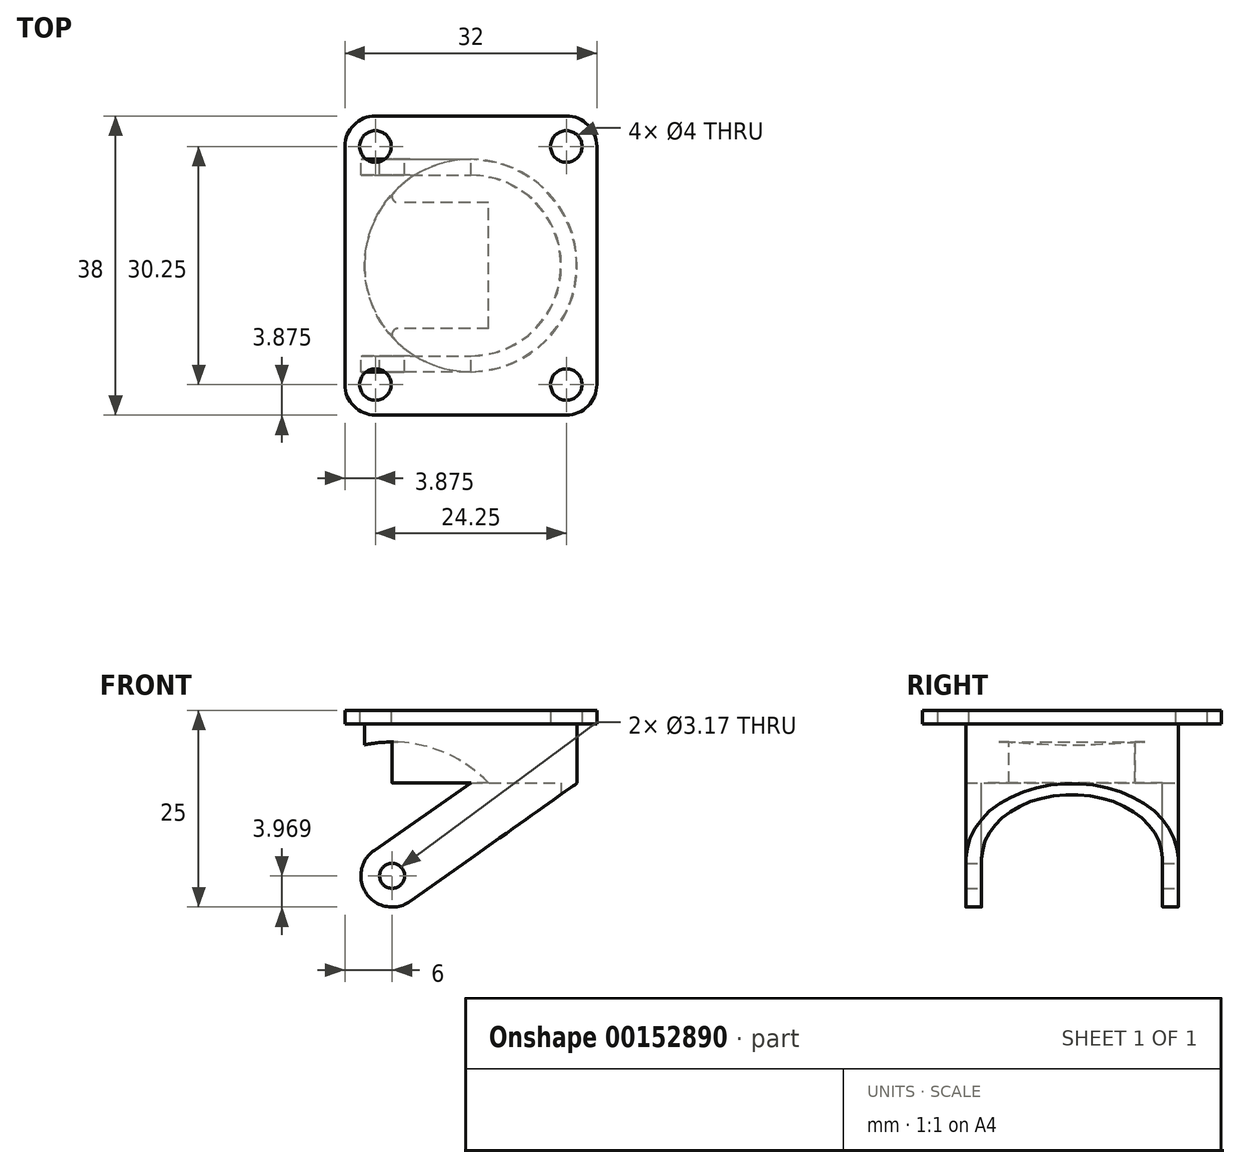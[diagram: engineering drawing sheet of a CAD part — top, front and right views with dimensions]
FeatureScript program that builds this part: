
annotation { "Feature Type Name" : "Feature", "Feature Type Description" : "" }
export const myFeature = defineFeature(function(context is Context, id is Id, definition is map)
    precondition{}
    {
        {
            var Q0;
            Q0=qCreatedBy(makeId("Top.planeOp"),FACE);
            var sketch = newSketch(context, id + "F0", { "sketchPlane" : qUnion([Q0])});
            skLineSegment(sketch, "E0.bottom", {"start": v(16, 19) * mm, "end": v(-16, 19) * mm});
            skLineSegment(sketch, "E0.top", {"start": v(16, -19) * mm, "end": v(-16, -19) * mm});
            skLineSegment(sketch, "E0.left", {"start": v(16, 19) * mm, "end": v(16, -19) * mm});
            skLineSegment(sketch, "E0.right", {"start": v(-16, 19) * mm, "end": v(-16, -19) * mm});
            skPoint(sketch, "E0.middle", {"position": v(0, 0) * mm});
            skLineSegment(sketch, "E1.bottom", {"start": v(12.12, 15.12) * mm, "end": v(-12.12, 15.12) * mm, "construction": true});
            skLineSegment(sketch, "E1.top", {"start": v(12.12, -15.12) * mm, "end": v(-12.12, -15.13) * mm, "construction": true});
            skLineSegment(sketch, "E1.left", {"start": v(12.12, 15.12) * mm, "end": v(12.13, -15.12) * mm, "construction": true});
            skLineSegment(sketch, "E1.right", {"start": v(-12.12, 15.12) * mm, "end": v(-12.12, -15.12) * mm, "construction": true});
            skLineSegment(sketch, "E2", {"start": v(12.12, 15.12) * mm, "end": v(12.12, 19) * mm, "construction": true});
            skLineSegment(sketch, "E3", {"start": v(12.12, 15.12) * mm, "end": v(16, 15.12) * mm, "construction": true});
            skCircle(sketch, "E4", {"center": v(12.12, 15.12) * mm, "radius": 2 * mm});
            skCircle(sketch, "E5", {"center": v(-12.12, 15.12) * mm, "radius": 2 * mm});
            skCircle(sketch, "E6", {"center": v(-12.12, -15.13) * mm, "radius": 2 * mm});
            skCircle(sketch, "E7", {"center": v(12.12, -15.12) * mm, "radius": 2 * mm});
            skSolve(sketch);
        }
        {
            var Q0;
            Q0 = qSketchRegion(id + "F0", true);
            extrude(context, id + "F1", {"entities" : qUnion([Q0]), "depth" : 1.75 * mm});
        }
        {
            var Q0;
            Q0=makeQuery(id+"F1.opExtrude","SWEPT_EDGE",EDGE,{"disambiguationData":[OSD([sQuery(id+"F0.wireOp",EDGE,"E0.bottom"),sQuery(id+"F0.wireOp",EDGE,"E0.left")])]});
            var Q1;
            Q1=makeQuery(id+"F1.opExtrude","SWEPT_EDGE",EDGE,{"disambiguationData":[OSD([sQuery(id+"F0.wireOp",EDGE,"E0.top"),sQuery(id+"F0.wireOp",EDGE,"E0.left")])]});
            var Q2;
            Q2=makeQuery(id+"F1.opExtrude","SWEPT_EDGE",EDGE,{"disambiguationData":[OSD([sQuery(id+"F0.wireOp",EDGE,"E0.top"),sQuery(id+"F0.wireOp",EDGE,"E0.right")])]});
            var Q3;
            Q3=makeQuery(id+"F1.opExtrude","SWEPT_EDGE",EDGE,{"disambiguationData":[OSD([sQuery(id+"F0.wireOp",EDGE,"E0.bottom"),sQuery(id+"F0.wireOp",EDGE,"E0.right")])]});
            fillet(context, id + "F2", {"entities" : qUnion([Q0, Q1, Q2, Q3]), "radius" : 3.87 * mm, "tangentPropagation" : true, "allowEdgeOverflow" : false});
        }
        {
            var Q0;
            Q0=makeQuery(id+"F1.opExtrude","CAP_FACE",FACE,{"disambiguationData":[OSD([sQuery(id+"F0.wireOp",EDGE,"E0.bottom"),sQuery(id+"F0.wireOp",EDGE,"E0.top"),sQuery(id+"F0.wireOp",EDGE,"E0.left"),sQuery(id+"F0.wireOp",EDGE,"E0.right"),sQuery(id+"F0.wireOp",EDGE,"E4"),sQuery(id+"F0.wireOp",EDGE,"E5"),sQuery(id+"F0.wireOp",EDGE,"E6"),sQuery(id+"F0.wireOp",EDGE,"E7")])],"isStart":true});
            var sketch = newSketch(context, id + "F3", { "sketchPlane" : qUnion([Q0])});
            skCircle(sketch, "E8", {"center": v(0, 0) * mm, "radius": 13.5 * mm});
            skSolve(sketch);
        }
        {
            var Q0;
            Q0 = qSketchRegion(id + "F3", true);
            extrude(context, id + "F4", {"entities" : qUnion([Q0]), "operationType" : NewBodyOperationType.ADD, "depth" : 7.5 * mm});
        }
        {
            var Q0;
            Q0=makeQuery(id+"F4.opExtrude","CAP_FACE",FACE,{"disambiguationData":[OSD([sQuery(id+"F3.wireOp",EDGE,"E8")])],"isStart":false});
            var sketch = newSketch(context, id + "F5", { "sketchPlane" : qUnion([Q0])});
            skLineSegment(sketch, "E9.bottom", {"start": v(0, 13.5) * mm, "end": v(-13.97, 13.5) * mm});
            skLineSegment(sketch, "E9.top", {"start": v(0, 11.5) * mm, "end": v(-13.97, 11.5) * mm});
            skLineSegment(sketch, "E9.left", {"start": v(0, 13.5) * mm, "end": v(0, 11.5) * mm});
            skLineSegment(sketch, "E9.right", {"start": v(-13.97, 13.5) * mm, "end": v(-13.97, 11.5) * mm});
            skLineSegment(sketch, "E10.bottom", {"start": v(0, -13.5) * mm, "end": v(-13.97, -13.5) * mm});
            skLineSegment(sketch, "E10.top", {"start": v(0, -11.5) * mm, "end": v(-13.97, -11.5) * mm});
            skLineSegment(sketch, "E10.left", {"start": v(0, -13.5) * mm, "end": v(0, -11.5) * mm});
            skLineSegment(sketch, "E10.right", {"start": v(-13.97, -13.5) * mm, "end": v(-13.97, -11.5) * mm});
            skArc(sketch, "E11", {"start": v(0, -11.5) * mm, "mid": v(11.5, 0) * mm, "end": v(0, 11.5) * mm});
            skArc(sketch, "E12", {"start": v(0, -13.5) * mm, "mid": v(13.5, 0) * mm, "end": v(0, 13.5) * mm});
            skLineSegment(sketch, "E13", {"start": v(-13.97, -12.5) * mm, "end": v(-10, -12.5) * mm, "construction": true});
            skLineSegment(sketch, "E14", {"start": v(-10, -12.5) * mm, "end": v(-10, 12.5) * mm, "construction": true});
            skLineSegment(sketch, "E15", {"start": v(-10, 12.5) * mm, "end": v(-13.97, 12.5) * mm, "construction": true});
            skLineSegment(sketch, "E16", {"start": v(-10, 0) * mm, "end": v(-26, 0) * mm, "construction": true});
            skSolve(sketch);
        }
        {
            var Q0;
            Q0 = qSketchRegion(id + "F5", true);
            extrude(context, id + "F6", {"entities" : qUnion([Q0]), "operationType" : NewBodyOperationType.ADD, "depth" : 15.75 * mm});
        }
        {
            var Q0;
            Q0=makeQuery(id+"F6.opExtrude","SWEPT_FACE",FACE,{"disambiguationData":[OSD([sQuery(id+"F5.wireOp",EDGE,"E10.bottom")])]});
            var sketch = newSketch(context, id + "F7", { "sketchPlane" : qUnion([Q0])});
            skArc(sketch, "E17", {"start": v(7.7, -22.52) * mm, "mid": v(13.25, -21.56) * mm, "end": v(12.26, -16.02) * mm});
            skLineSegment(sketch, "E18", {"start": v(12.26, -16.02) * mm, "end": v(0, -7.5) * mm});
            skLineSegment(sketch, "E19", {"start": v(7.7, -22.52) * mm, "end": v(-13.5, -7.5) * mm});
            skLineSegment(sketch, "E20.bottom", {"start": v(13.97, -7.5) * mm, "end": v(0, -7.5) * mm});
            skLineSegment(sketch, "E20.top", {"start": v(13.97, -23.25) * mm, "end": v(-13.5, -23.25) * mm});
            skLineSegment(sketch, "E20.left", {"start": v(13.97, -7.5) * mm, "end": v(13.97, -23.25) * mm});
            skLineSegment(sketch, "E20.right", {"start": v(-13.5, -7.5) * mm, "end": v(-13.5, -23.25) * mm});
            skLineSegment(sketch, "E21", {"start": v(0, -7.5) * mm, "end": v(-13.5, -7.5) * mm, "construction": true});
            skCircle(sketch, "E22", {"center": v(10, -19.28) * mm, "radius": 1.59 * mm});
            skSolve(sketch);
        }
        {
            var Q0;
            Q0 = qSketchRegion(id + "F7", true);
            var Q1;
            Q1=makeQuery(id+"F6.opExtrude","SWEPT_FACE",FACE,{"disambiguationData":[OSD([sQuery(id+"F5.wireOp",EDGE,"E9.bottom")])]});
            extrude(context, id + "F8", {"entities" : qUnion([Q0]), "operationType" : NewBodyOperationType.REMOVE, "endBound" : BoundingType.UP_TO_SURFACE, "oppositeDirection" : true, "endBoundEntityFace" : qUnion([Q1]), "depth" : 25.4 * mm});
        }
        {
            var Q0;
            Q0=qCreatedBy(makeId("Front.planeOp"),FACE);
            var sketch = newSketch(context, id + "F9", { "sketchPlane" : qUnion([Q0])});
            skCircle(sketch, "E23", {"center": v(-10, -19.28) * mm, "radius": 17 * mm});
            skSolve(sketch);
        }
        {
            var Q0;
            Q0 = qSketchRegion(id + "F9", true);
            var Q1;
            Q1=makeQuery(id+"F6.opExtrude","SWEPT_FACE",FACE,{"disambiguationData":[OSD([sQuery(id+"F5.wireOp",EDGE,"E11")])]});
            var Q2;
            Q2=makeQuery(id+"F6.opExtrude","SWEPT_FACE",FACE,{"disambiguationData":[OSD([sQuery(id+"F5.wireOp",EDGE,"E10.top")])]});
            extrude(context, id + "F10", {"entities" : qUnion([Q0]), "operationType" : NewBodyOperationType.REMOVE, "endBound" : BoundingType.SYMMETRIC, "endBoundEntityFace" : qUnion([Q1]), "depth" : 16 * mm, "hasSecondDirection" : true, "secondDirectionBound" : SecondDirectionBoundingType.UP_TO_SURFACE, "secondDirectionOppositeDirection" : true, "secondDirectionBoundEntityFace" : qUnion([Q2]), "secondDirectionDepth" : 25.4 * mm});
        }
        {
            var Q0;
            Q0=makeQuery(id+"F10.boolean.opBoolean","INTERSECT",EDGE,{"derivedFrom":[makeQuery(id+"F6.boolean.opBoolean","MERGE",FACE,{"derivedFrom":[makeQuery(id+"F4.opExtrude","SWEPT_FACE",FACE,{"disambiguationData":[OSD([sQuery(id+"F3.wireOp",EDGE,"E8")])]}),makeQuery(id+"F6.opExtrude","SWEPT_FACE",FACE,{"disambiguationData":[OSD([sQuery(id+"F5.wireOp",EDGE,"E12")])]})]}),makeQuery(id+"F10.opExtrude","CAP_FACE",FACE,{"disambiguationData":[OSD([sQuery(id+"F9.wireOp",EDGE,"E23")])],"isStart":true})]});
            var Q1;
            Q1=makeQuery(id+"F10.boolean.opBoolean","INTERSECT",EDGE,{"derivedFrom":[makeQuery(id+"F6.boolean.opBoolean","MERGE",FACE,{"derivedFrom":[makeQuery(id+"F4.opExtrude","SWEPT_FACE",FACE,{"disambiguationData":[OSD([sQuery(id+"F3.wireOp",EDGE,"E8")])]}),makeQuery(id+"F6.opExtrude","SWEPT_FACE",FACE,{"disambiguationData":[OSD([sQuery(id+"F5.wireOp",EDGE,"E12")])]})]}),makeQuery(id+"F10.opExtrude","CAP_FACE",FACE,{"disambiguationData":[OSD([sQuery(id+"F9.wireOp",EDGE,"E23")])],"isStart":false})]});
            fillet(context, id + "F11", {"entities" : qUnion([Q0, Q1]), "radius" : 0.76 * mm, "tangentPropagation" : true, "allowEdgeOverflow" : false});
        }
    });
